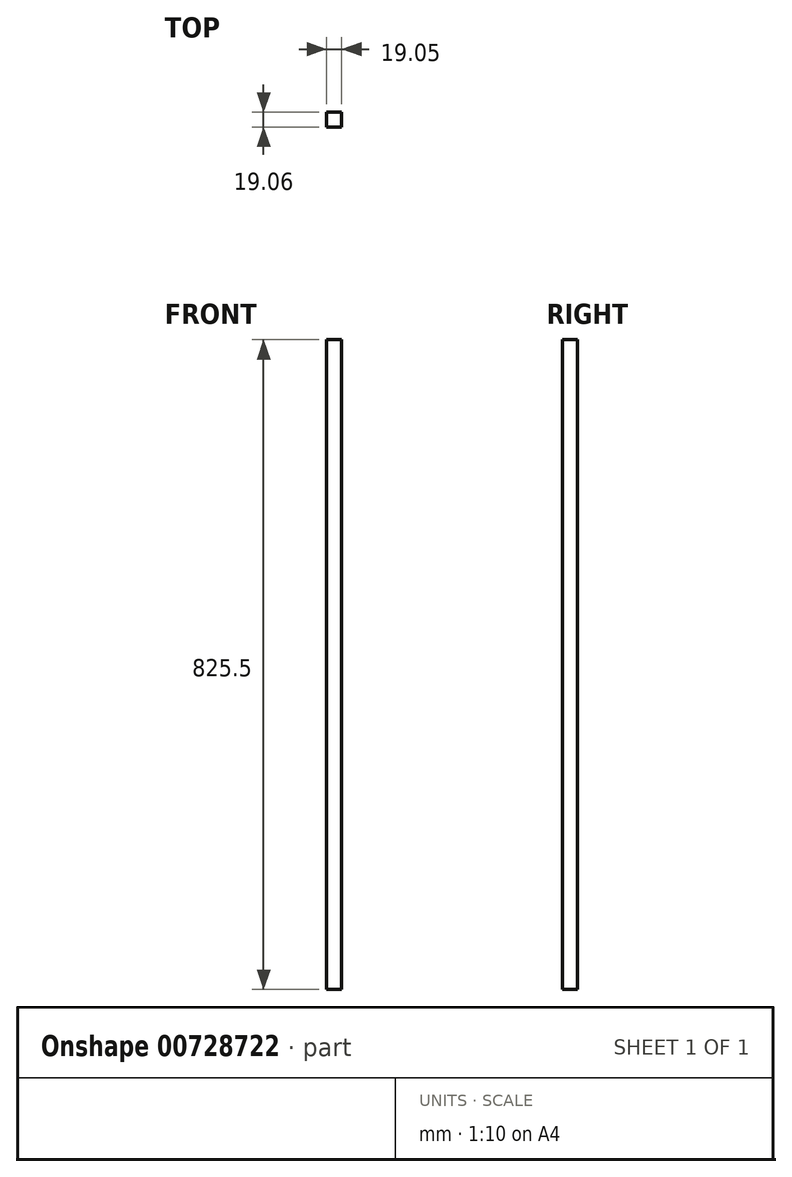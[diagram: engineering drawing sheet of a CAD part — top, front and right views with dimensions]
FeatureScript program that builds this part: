
annotation { "Feature Type Name" : "Feature", "Feature Type Description" : "" }
export const myFeature = defineFeature(function(context is Context, id is Id, definition is map)
    precondition{}
    {
        {
            var Q0;
            Q0=qCreatedBy(makeId("Right.planeOp"),FACE);
            var sketch = newSketch(context, id + "F0", { "sketchPlane" : qUnion([Q0])});
            skLineSegment(sketch, "E0.bottom", {"start": v(9.52, 412.75) * mm, "end": v(-9.53, 412.75) * mm});
            skLineSegment(sketch, "E0.top", {"start": v(9.53, -412.75) * mm, "end": v(-9.52, -412.75) * mm});
            skLineSegment(sketch, "E0.left", {"start": v(9.52, 412.75) * mm, "end": v(9.53, -412.75) * mm});
            skLineSegment(sketch, "E0.right", {"start": v(-9.53, 412.75) * mm, "end": v(-9.52, -412.75) * mm});
            skPoint(sketch, "E0.middle", {"position": v(0, 0) * mm});
            skSolve(sketch);
        }
        {
            var Q0;
            Q0 = qSketchRegion(id + "F0", true);
            extrude(context, id + "F1", {"entities" : qUnion([Q0]), "depth" : 19.05 * mm, "offsetDistance" : 25.4 * mm});
        }
    });
